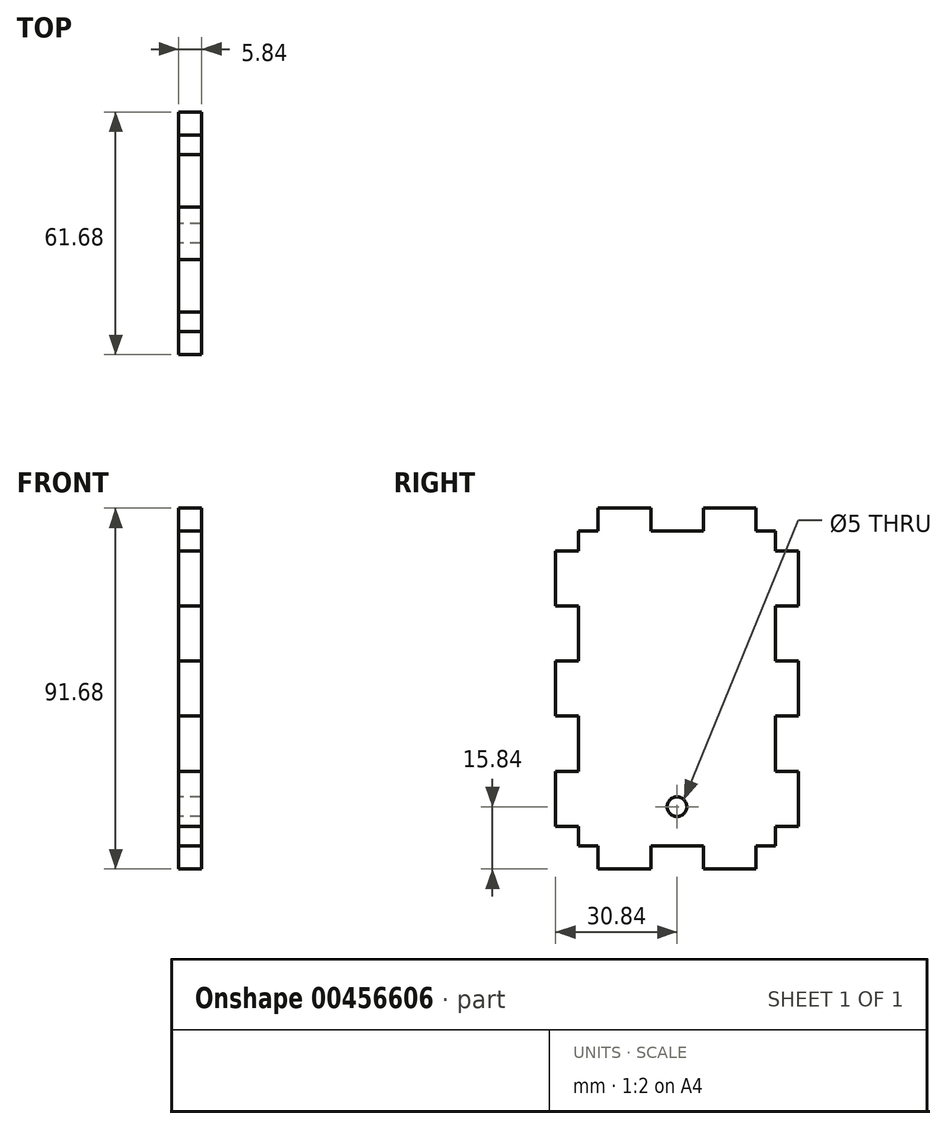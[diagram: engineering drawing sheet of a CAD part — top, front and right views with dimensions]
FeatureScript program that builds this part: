
annotation { "Feature Type Name" : "Feature", "Feature Type Description" : "" }
export const myFeature = defineFeature(function(context is Context, id is Id, definition is map)
    precondition{}
    {
        {
            var Q0;
            Q0=qCreatedBy(makeId("Right.planeOp"),FACE);
            var sketch = newSketch(context, id + "F0", { "sketchPlane" : qUnion([Q0])});
            skLineSegment(sketch, "E0.bottom", {"start": v(-25, -40) * mm, "end": v(-20, -40) * mm});
            skLineSegment(sketch, "E0.top", {"start": v(-25, 40) * mm, "end": v(-20, 40) * mm});
            skLineSegment(sketch, "E0.left", {"start": v(-25, -40) * mm, "end": v(-25, -35) * mm});
            skLineSegment(sketch, "E0.right", {"start": v(25, -40) * mm, "end": v(25, -35) * mm});
            skLineSegment(sketch, "E1.bottom", {"start": v(-20, 45.84) * mm, "end": v(-6.67, 45.84) * mm});
            skLineSegment(sketch, "E1.top", {"start": v(-20, -45.84) * mm, "end": v(-6.67, -45.84) * mm});
            skLineSegment(sketch, "E1.left", {"start": v(-30.84, 35) * mm, "end": v(-30.84, 21) * mm});
            skLineSegment(sketch, "E1.right", {"start": v(30.84, 35) * mm, "end": v(30.84, 21) * mm});
            skLineSegment(sketch, "E2.top", {"start": v(-30.84, 35) * mm, "end": v(-25, 35) * mm});
            skLineSegment(sketch, "E2.right", {"start": v(-20, 45.84) * mm, "end": v(-20, 40) * mm});
            skLineSegment(sketch, "E3.top", {"start": v(30.84, 35) * mm, "end": v(25, 35) * mm});
            skLineSegment(sketch, "E3.right", {"start": v(20, 45.84) * mm, "end": v(20, 40) * mm});
            skLineSegment(sketch, "E4.bottom", {"start": v(-6.67, 40) * mm, "end": v(6.67, 40) * mm});
            skLineSegment(sketch, "E4.left", {"start": v(-6.67, 40) * mm, "end": v(-6.67, 45.84) * mm});
            skLineSegment(sketch, "E4.right", {"start": v(6.67, 40) * mm, "end": v(6.67, 45.84) * mm});
            skLineSegment(sketch, "E5.top", {"start": v(-30.84, -35) * mm, "end": v(-25, -35) * mm});
            skLineSegment(sketch, "E5.right", {"start": v(-20, -45.84) * mm, "end": v(-20, -40) * mm});
            skLineSegment(sketch, "E6.top", {"start": v(30.84, -35) * mm, "end": v(25, -35) * mm});
            skLineSegment(sketch, "E6.right", {"start": v(20, -45.84) * mm, "end": v(20, -40) * mm});
            skLineSegment(sketch, "E7.top", {"start": v(-6.67, -40) * mm, "end": v(6.67, -40) * mm});
            skLineSegment(sketch, "E7.left", {"start": v(-6.67, -45.84) * mm, "end": v(-6.67, -40) * mm});
            skLineSegment(sketch, "E7.right", {"start": v(6.67, -45.84) * mm, "end": v(6.67, -40) * mm});
            skLineSegment(sketch, "E8.bottom", {"start": v(-30.84, 21) * mm, "end": v(-25, 21) * mm});
            skLineSegment(sketch, "E8.top", {"start": v(-30.84, 7) * mm, "end": v(-25, 7) * mm});
            skLineSegment(sketch, "E8.right", {"start": v(-25, 21) * mm, "end": v(-25, 7) * mm});
            skLineSegment(sketch, "E9.bottom", {"start": v(-30.84, -7) * mm, "end": v(-25, -7) * mm});
            skLineSegment(sketch, "E9.top", {"start": v(-30.84, -21) * mm, "end": v(-25, -21) * mm});
            skLineSegment(sketch, "E9.right", {"start": v(-25, -7) * mm, "end": v(-25, -21) * mm});
            skLineSegment(sketch, "E10.bottom", {"start": v(25, 21) * mm, "end": v(30.84, 21) * mm});
            skLineSegment(sketch, "E10.top", {"start": v(25, 7) * mm, "end": v(30.84, 7) * mm});
            skLineSegment(sketch, "E10.left", {"start": v(25, 21) * mm, "end": v(25, 7) * mm});
            skLineSegment(sketch, "E11.bottom", {"start": v(25, -7) * mm, "end": v(30.84, -7) * mm});
            skLineSegment(sketch, "E11.top", {"start": v(25, -21) * mm, "end": v(30.84, -21) * mm});
            skLineSegment(sketch, "E11.left", {"start": v(25, -7) * mm, "end": v(25, -21) * mm});
            skLineSegment(sketch, "E12.trimOffspring", {"start": v(6.67, 45.84) * mm, "end": v(20, 45.84) * mm});
            skLineSegment(sketch, "E13.trimOffspring", {"start": v(30.84, 7) * mm, "end": v(30.84, -7) * mm});
            skLineSegment(sketch, "E14.trimOffspring", {"start": v(30.84, -21) * mm, "end": v(30.84, -35) * mm});
            skLineSegment(sketch, "E15.trimOffspring", {"start": v(-30.84, 7) * mm, "end": v(-30.84, -7) * mm});
            skLineSegment(sketch, "E16.trimOffspring", {"start": v(-25, 35) * mm, "end": v(-25, 40) * mm});
            skLineSegment(sketch, "E17.trimOffspring", {"start": v(25, 35) * mm, "end": v(25, 40) * mm});
            skLineSegment(sketch, "E18.trimOffspring", {"start": v(20, 40) * mm, "end": v(25, 40) * mm});
            skLineSegment(sketch, "E19.trimOffspring", {"start": v(-25, 7) * mm, "end": v(-25, 21) * mm});
            skLineSegment(sketch, "E20.trimOffspring", {"start": v(-30.84, -21) * mm, "end": v(-30.84, -35) * mm});
            skLineSegment(sketch, "E21.trimOffspring", {"start": v(6.67, -45.84) * mm, "end": v(20, -45.84) * mm});
            skLineSegment(sketch, "E22.trimOffspring", {"start": v(25, 7) * mm, "end": v(25, 21) * mm});
            skLineSegment(sketch, "E23.trimOffspring", {"start": v(25, -21) * mm, "end": v(25, -7) * mm});
            skLineSegment(sketch, "E24.trimOffspring", {"start": v(-25, -21) * mm, "end": v(-25, -7) * mm});
            skLineSegment(sketch, "E25.trimOffspring", {"start": v(20, -40) * mm, "end": v(25, -40) * mm});
            skCircle(sketch, "E26", {"center": v(0, -30) * mm, "radius": 2.5 * mm});
            skSolve(sketch);
        }
        {
            var Q0;
            Q0 = qSketchRegion(id + "F0", true);
            extrude(context, id + "F1", {"entities" : qUnion([Q0]), "depth" : 5.84 * mm});
        }
    });
